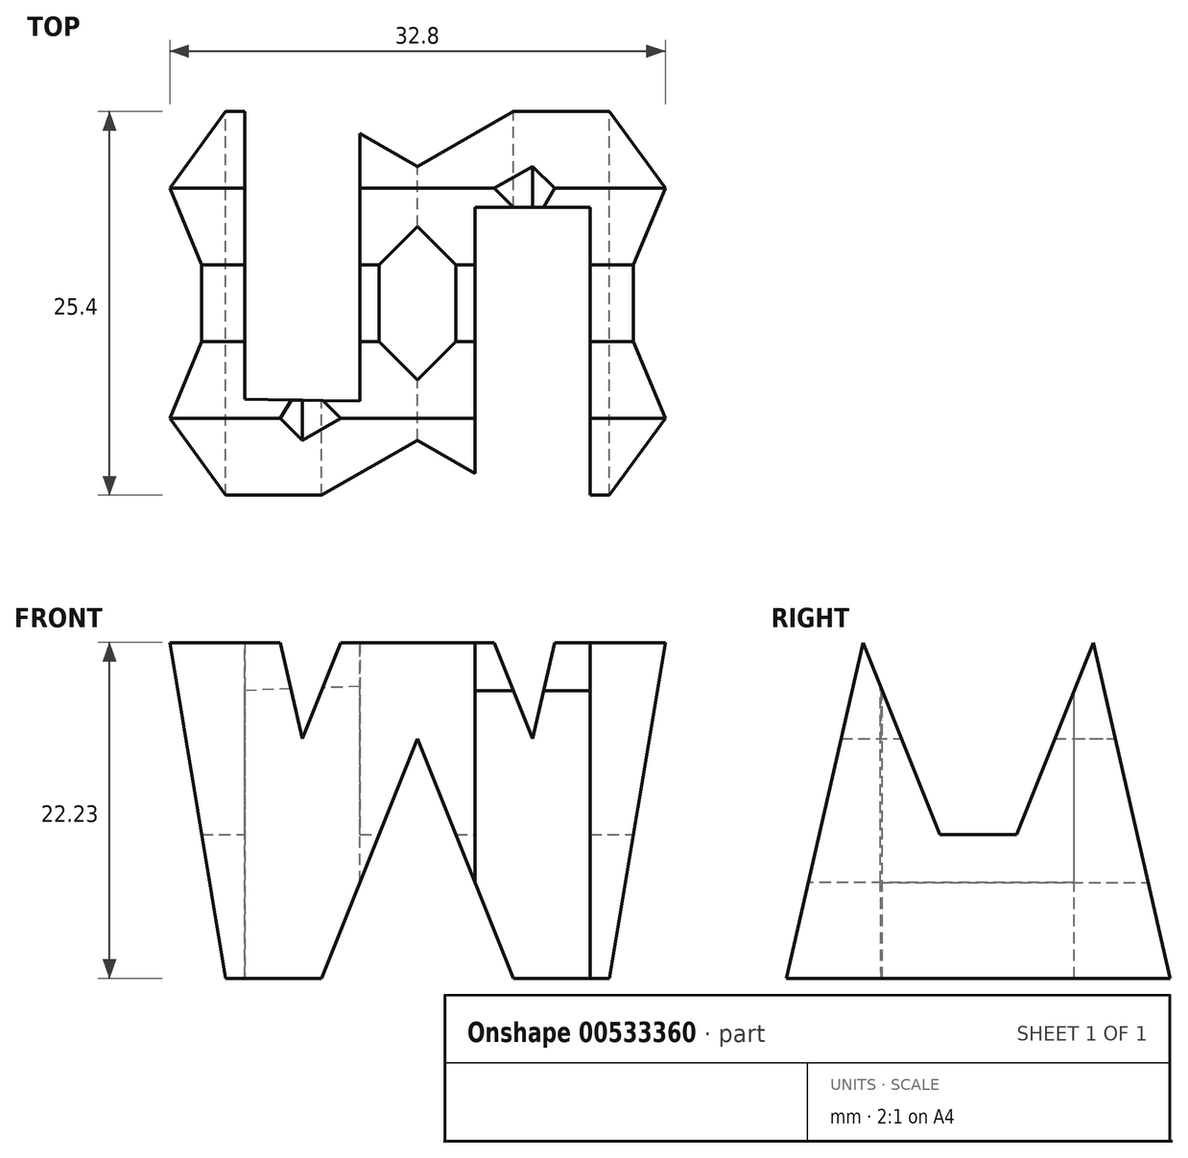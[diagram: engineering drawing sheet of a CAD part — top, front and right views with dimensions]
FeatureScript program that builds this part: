
annotation { "Feature Type Name" : "Feature", "Feature Type Description" : "" }
export const myFeature = defineFeature(function(context is Context, id is Id, definition is map)
    precondition{}
    {
        {
            var Q0;
            Q0=qCreatedBy(makeId("Right.planeOp"),FACE);
            var sketch = newSketch(context, id + "F0", { "sketchPlane" : qUnion([Q0])});
            skLineSegment(sketch, "E0", {"start": v(0, 0) * mm, "end": v(0, 38.1) * mm});
            skLineSegment(sketch, "E1", {"start": v(0, 38.1) * mm, "end": v(38.1, 38.1) * mm});
            skLineSegment(sketch, "E2", {"start": v(38.1, 38.1) * mm, "end": v(38.1, 0) * mm});
            skLineSegment(sketch, "E3", {"start": v(0, 0) * mm, "end": v(38.1, 0) * mm});
            skSolve(sketch);
        }
        {
            var Q0;
            Q0 = qSketchRegion(id + "F0", true);
            extrude(context, id + "F1", {"entities" : qUnion([Q0]), "depth" : 38.1 * mm, "offsetDistance" : 25.4 * mm});
        }
        {
            var Q0;
            Q0=qCreatedBy(makeId("Right.planeOp"),FACE);
            cPlane(context, id + "F2", {"entities" : qUnion([Q0]), "cplaneType" : CPlaneType.OFFSET, "offset" : 38.1 * mm, "width" : 152.4 * mm, "height" : 152.4 * mm});
        }
        {
            var Q0;
            Q0=qCreatedBy(makeId("Top.planeOp"),FACE);
            cPlane(context, id + "F3", {"entities" : qUnion([Q0]), "cplaneType" : CPlaneType.OFFSET, "offset" : 38.1 * mm, "width" : 152.4 * mm, "height" : 152.4 * mm});
        }
        {
            var Q0;
            Q0=qCreatedBy(makeId("Front.planeOp"),FACE);
            cPlane(context, id + "F4", {"entities" : qUnion([Q0]), "cplaneType" : CPlaneType.OFFSET, "offset" : 38.1 * mm, "oppositeDirection" : true, "width" : 152.4 * mm, "height" : 152.4 * mm});
        }
        {
            var Q0;
            Q0=qCreatedBy(id+"F4.planeOp",FACE);
            var sketch = newSketch(context, id + "F5", { "sketchPlane" : qUnion([Q0])});
            skLineSegment(sketch, "E4", {"start": v(0, 0) * mm, "end": v(0, 38.1) * mm});
            skLineSegment(sketch, "E5", {"start": v(38.1, 38.1) * mm, "end": v(38.1, 0) * mm});
            skLineSegment(sketch, "E6", {"start": v(38.1, 38.1) * mm, "end": v(31.75, 0) * mm});
            skLineSegment(sketch, "E7", {"start": v(31.75, 38.1) * mm, "end": v(26.67, 15.87) * mm});
            skLineSegment(sketch, "E8", {"start": v(26.67, 15.88) * mm, "end": v(21.59, 28.58) * mm});
            skLineSegment(sketch, "E9", {"start": v(21.59, 28.58) * mm, "end": v(16.5, 28.58) * mm});
            skLineSegment(sketch, "E10", {"start": v(16.5, 28.58) * mm, "end": v(11.43, 15.88) * mm});
            skLineSegment(sketch, "E11", {"start": v(11.43, 15.88) * mm, "end": v(6.35, 38.1) * mm});
            skLineSegment(sketch, "E12", {"start": v(6.35, 0) * mm, "end": v(0, 38.1) * mm});
            skLineSegment(sketch, "E13", {"start": v(25.4, 0) * mm, "end": v(19.05, 15.88) * mm});
            skLineSegment(sketch, "E14", {"start": v(19.05, 15.88) * mm, "end": v(12.7, 0) * mm});
            skLineSegment(sketch, "E15", {"start": v(12.7, 0) * mm, "end": v(6.35, 0) * mm});
            skLineSegment(sketch, "E16", {"start": v(25.4, 0) * mm, "end": v(12.7, 0) * mm});
            skLineSegment(sketch, "E17", {"start": v(38.1, 0) * mm, "end": v(0, 0) * mm});
            skLineSegment(sketch, "E18", {"start": v(38.1, 38.1) * mm, "end": v(0, 38.1) * mm});
            skSolve(sketch);
        }
        {
            var Q0;
            {var subQ0=sQuery(id+"F5.wireOp",EDGE,"E5");Q0=makeQuery(id+"F5.imprint","IMPRINT",FACE,{"disambiguationData":[TD([[makeQuery(id+"F5.imprint","IMPRINT",EDGE,{"derivedFrom":subQ0}),-1.0]])]});}
            var Q1;
            {var subQ1=sQuery(id+"F5.wireOp",EDGE,"E7");Q1=makeQuery(id+"F5.imprint","IMPRINT",FACE,{"disambiguationData":[TD([[makeQuery(id+"F5.imprint","IMPRINT",EDGE,{"derivedFrom":subQ1}),-1.0]])]});}
            var Q2;
            {var subQ0=sQuery(id+"F5.wireOp",EDGE,"E13");Q2=makeQuery(id+"F5.imprint","IMPRINT",FACE,{"disambiguationData":[TD([[makeQuery(id+"F5.imprint","IMPRINT",EDGE,{"derivedFrom":subQ0}),1.0]])]});}
            var Q3;
            {var subQ0=sQuery(id+"F5.wireOp",EDGE,"E4");Q3=makeQuery(id+"F5.imprint","IMPRINT",FACE,{"disambiguationData":[TD([[makeQuery(id+"F5.imprint","IMPRINT",EDGE,{"derivedFrom":subQ0}),-1.0]])]});}
            extrude(context, id + "F6", {"entities" : qUnion([Q0, Q1, Q2, Q3]), "operationType" : NewBodyOperationType.REMOVE, "depth" : 38.1 * mm, "offsetDistance" : 25.4 * mm});
        }
        {
            var Q0;
            Q0=qCreatedBy(id+"F2.planeOp",FACE);
            var sketch = newSketch(context, id + "F7", { "sketchPlane" : qUnion([Q0])});
            skLineSegment(sketch, "E19", {"start": v(0, 0) * mm, "end": v(0, 38.1) * mm});
            skLineSegment(sketch, "E20", {"start": v(0, 38.1) * mm, "end": v(38.1, 38.1) * mm});
            skLineSegment(sketch, "E21", {"start": v(38.1, 38.1) * mm, "end": v(38.1, 0) * mm});
            skLineSegment(sketch, "E22", {"start": v(38.1, 0) * mm, "end": v(0, 0) * mm});
            skLineSegment(sketch, "E23", {"start": v(0, 0) * mm, "end": v(6.35, 38.1) * mm});
            skLineSegment(sketch, "E24", {"start": v(6.35, 38.1) * mm, "end": v(12.7, 38.1) * mm});
            skLineSegment(sketch, "E25", {"start": v(12.7, 38.1) * mm, "end": v(19.05, 22.23) * mm});
            skLineSegment(sketch, "E26", {"start": v(19.05, 22.23) * mm, "end": v(25.4, 38.1) * mm});
            skLineSegment(sketch, "E27", {"start": v(25.4, 38.1) * mm, "end": v(31.75, 38.1) * mm});
            skLineSegment(sketch, "E28", {"start": v(31.75, 38.1) * mm, "end": v(38.1, 0) * mm});
            skLineSegment(sketch, "E29", {"start": v(38.1, 0) * mm, "end": v(31.75, 0) * mm});
            skLineSegment(sketch, "E30", {"start": v(31.75, 0) * mm, "end": v(26.67, 22.22) * mm});
            skLineSegment(sketch, "E31", {"start": v(26.67, 22.23) * mm, "end": v(21.6, 9.53) * mm});
            skLineSegment(sketch, "E32", {"start": v(21.59, 9.53) * mm, "end": v(16.51, 9.53) * mm});
            skLineSegment(sketch, "E33", {"start": v(16.51, 9.53) * mm, "end": v(11.43, 22.23) * mm});
            skLineSegment(sketch, "E34", {"start": v(11.43, 22.23) * mm, "end": v(6.35, 0) * mm});
            skLineSegment(sketch, "E35", {"start": v(6.35, 0) * mm, "end": v(0, 0) * mm});
            skSolve(sketch);
        }
        {
            var Q0;
            {var subQ0=sQuery(id+"F7.wireOp",EDGE,"E19");Q0=makeQuery(id+"F7.imprint","IMPRINT",FACE,{"disambiguationData":[TD([[makeQuery(id+"F7.imprint","IMPRINT",EDGE,{"derivedFrom":subQ0}),-1.0]])]});}
            var Q1;
            {var subQ0=sQuery(id+"F7.wireOp",EDGE,"E25");Q1=makeQuery(id+"F7.imprint","IMPRINT",FACE,{"disambiguationData":[TD([[makeQuery(id+"F7.imprint","IMPRINT",EDGE,{"derivedFrom":subQ0}),1.0]])]});}
            var Q2;
            {var subQ0=sQuery(id+"F7.wireOp",EDGE,"E21");Q2=makeQuery(id+"F7.imprint","IMPRINT",FACE,{"disambiguationData":[TD([[makeQuery(id+"F7.imprint","IMPRINT",EDGE,{"derivedFrom":subQ0}),-1.0]])]});}
            var Q3;
            Q3=makeQuery(id+"F7.imprint","IMPRINT",FACE,{"disambiguationData":[TD([[makeQuery(id+"F7.imprint","IMPRINT",EDGE,{"derivedFrom":sQuery(id+"F7.wireOp",EDGE,"E22")}),-1.0]])]});
            extrude(context, id + "F8", {"entities" : qUnion([Q0, Q1, Q2, Q3]), "operationType" : NewBodyOperationType.REMOVE, "oppositeDirection" : true, "depth" : 38.1 * mm, "offsetDistance" : 25.4 * mm});
        }
        {
            var Q0;
            Q0=qCreatedBy(id+"F3.planeOp",FACE);
            var sketch = newSketch(context, id + "F9", { "sketchPlane" : qUnion([Q0])});
            skLineSegment(sketch, "E36", {"start": v(0, 0) * mm, "end": v(38.1, 0) * mm});
            skLineSegment(sketch, "E37", {"start": v(38.1, 0) * mm, "end": v(38.1, 38.1) * mm});
            skLineSegment(sketch, "E38", {"start": v(38.1, 38.1) * mm, "end": v(0, 38.1) * mm});
            skLineSegment(sketch, "E39", {"start": v(0, 38.1) * mm, "end": v(0, 0) * mm});
            skLineSegment(sketch, "E40", {"start": v(30.48, 25.4) * mm, "end": v(30.48, 0) * mm});
            skLineSegment(sketch, "E41", {"start": v(30.48, 0) * mm, "end": v(22.86, 0) * mm});
            skLineSegment(sketch, "E42", {"start": v(22.86, 0) * mm, "end": v(22.86, 25.4) * mm});
            skLineSegment(sketch, "E43", {"start": v(22.86, 25.4) * mm, "end": v(30.48, 25.4) * mm});
            skLineSegment(sketch, "E44", {"start": v(7.62, 12.7) * mm, "end": v(7.62, 38.1) * mm});
            skLineSegment(sketch, "E45", {"start": v(7.62, 38.1) * mm, "end": v(15.24, 38.1) * mm});
            skLineSegment(sketch, "E46", {"start": v(15.24, 38.1) * mm, "end": v(15.24, 12.6) * mm});
            skLineSegment(sketch, "E47", {"start": v(15.24, 12.6) * mm, "end": v(7.62, 12.7) * mm});
            skSolve(sketch);
        }
        {
            var Q0;
            Q0=makeQuery(id+"F9.imprint","IMPRINT",FACE,{"disambiguationData":[TD([[makeQuery(id+"F9.imprint","IMPRINT",EDGE,{"derivedFrom":sQuery(id+"F9.wireOp",EDGE,"E40")}),-1.0]])]});
            var Q1;
            Q1=makeQuery(id+"F9.imprint","IMPRINT",FACE,{"disambiguationData":[TD([[makeQuery(id+"F9.imprint","IMPRINT",EDGE,{"derivedFrom":sQuery(id+"F9.wireOp",EDGE,"E44")}),-1.0]])]});
            extrude(context, id + "F10", {"entities" : qUnion([Q0, Q1]), "operationType" : NewBodyOperationType.REMOVE, "oppositeDirection" : true, "depth" : 38.1 * mm, "offsetDistance" : 25.4 * mm});
        }
    });
